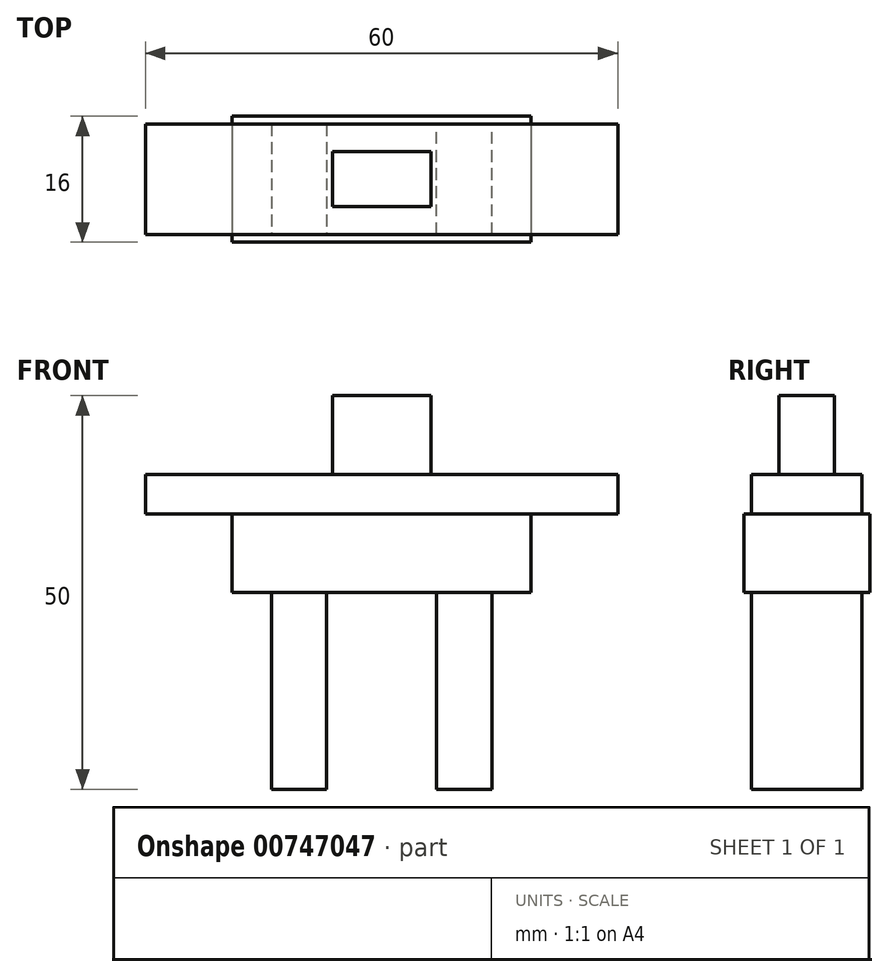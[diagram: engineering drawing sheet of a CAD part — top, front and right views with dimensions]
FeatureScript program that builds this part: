
annotation { "Feature Type Name" : "Feature", "Feature Type Description" : "" }
export const myFeature = defineFeature(function(context is Context, id is Id, definition is map)
    precondition{}
    {
        {
            var Q0;
            Q0=qCreatedBy(makeId("Top.planeOp"),FACE);
            var sketch = newSketch(context, id + "F0", { "sketchPlane" : qUnion([Q0])});
            skLineSegment(sketch, "E0.bottom", {"start": v(-14, 7) * mm, "end": v(-7, 7) * mm});
            skLineSegment(sketch, "E0.top", {"start": v(-14, -7) * mm, "end": v(-7, -7) * mm});
            skLineSegment(sketch, "E0.left", {"start": v(-14, 7) * mm, "end": v(-14, -7) * mm});
            skLineSegment(sketch, "E0.right", {"start": v(-7, 7) * mm, "end": v(-7, -7) * mm});
            skPoint(sketch, "E1", {"position": v(-14, 0) * mm});
            skSolve(sketch);
        }
        {
            var Q0;
            Q0 = qSketchRegion(id + "F0", true);
            extrude(context, id + "F1", {"entities" : qUnion([Q0]), "depth" : 25 * mm, "offsetDistance" : 25.4 * mm});
        }
        {
            var Q0;
            Q0=makeQuery(id+"F1.opExtrude","CAP_FACE",FACE,{"disambiguationData":[OSD([sQuery(id+"F0.wireOp",EDGE,"E0.bottom"),sQuery(id+"F0.wireOp",EDGE,"E0.top"),sQuery(id+"F0.wireOp",EDGE,"E0.left"),sQuery(id+"F0.wireOp",EDGE,"E0.right")])],"isStart":false});
            var sketch = newSketch(context, id + "F2", { "sketchPlane" : qUnion([Q0])});
            skLineSegment(sketch, "E2.bottom", {"start": v(-19, 8) * mm, "end": v(19, 8) * mm});
            skLineSegment(sketch, "E2.top", {"start": v(-19, -8) * mm, "end": v(19, -8) * mm});
            skLineSegment(sketch, "E2.left", {"start": v(-19, 8) * mm, "end": v(-19, -8) * mm});
            skLineSegment(sketch, "E2.right", {"start": v(19, 8) * mm, "end": v(19, -8) * mm});
            skPoint(sketch, "E3", {"position": v(0, 8) * mm});
            skPoint(sketch, "E4", {"position": v(-19, 0) * mm});
            skSolve(sketch);
        }
        {
            var Q0;
            Q0 = qSketchRegion(id + "F2", true);
            extrude(context, id + "F3", {"entities" : qUnion([Q0]), "operationType" : NewBodyOperationType.ADD, "depth" : 10 * mm, "offsetDistance" : 25 * mm});
        }
        {
            var Q0;
            Q0=makeQuery(id+"F3.opExtrude","CAP_FACE",FACE,{"disambiguationData":[OSD([sQuery(id+"F2.wireOp",EDGE,"E2.bottom"),sQuery(id+"F2.wireOp",EDGE,"E2.top"),sQuery(id+"F2.wireOp",EDGE,"E2.left"),sQuery(id+"F2.wireOp",EDGE,"E2.right")])],"isStart":false});
            var sketch = newSketch(context, id + "F4", { "sketchPlane" : qUnion([Q0])});
            skLineSegment(sketch, "E5.bottom", {"start": v(-30, 7) * mm, "end": v(30, 7) * mm});
            skLineSegment(sketch, "E5.top", {"start": v(-30, -7) * mm, "end": v(30, -7) * mm});
            skLineSegment(sketch, "E5.left", {"start": v(-30, 7) * mm, "end": v(-30, -7) * mm});
            skLineSegment(sketch, "E5.right", {"start": v(30, 7) * mm, "end": v(30, -7) * mm});
            skPoint(sketch, "E6", {"position": v(0, 7) * mm});
            skPoint(sketch, "E7", {"position": v(30, 0) * mm});
            skSolve(sketch);
        }
        {
            var Q0;
            Q0 = qSketchRegion(id + "F4", true);
            extrude(context, id + "F5", {"entities" : qUnion([Q0]), "operationType" : NewBodyOperationType.ADD, "depth" : 5 * mm, "offsetDistance" : 25 * mm});
        }
        {
            var Q0;
            Q0=makeQuery(id+"F5.opExtrude","CAP_FACE",FACE,{"disambiguationData":[OSD([sQuery(id+"F4.wireOp",EDGE,"E5.bottom"),sQuery(id+"F4.wireOp",EDGE,"E5.top"),sQuery(id+"F4.wireOp",EDGE,"E5.left"),sQuery(id+"F4.wireOp",EDGE,"E5.right")])],"isStart":false});
            var sketch = newSketch(context, id + "F6", { "sketchPlane" : qUnion([Q0])});
            skLineSegment(sketch, "E8.bottom", {"start": v(-6.25, 3.5) * mm, "end": v(6.25, 3.5) * mm});
            skLineSegment(sketch, "E8.top", {"start": v(-6.25, -3.5) * mm, "end": v(6.25, -3.5) * mm});
            skLineSegment(sketch, "E8.left", {"start": v(-6.25, 3.5) * mm, "end": v(-6.25, -3.5) * mm});
            skLineSegment(sketch, "E8.right", {"start": v(6.25, 3.5) * mm, "end": v(6.25, -3.5) * mm});
            skPoint(sketch, "E9", {"position": v(0, 3.5) * mm});
            skPoint(sketch, "E10", {"position": v(6.25, 0) * mm});
            skSolve(sketch);
        }
        {
            var Q0;
            Q0 = qSketchRegion(id + "F6", true);
            extrude(context, id + "F7", {"entities" : qUnion([Q0]), "operationType" : NewBodyOperationType.ADD, "depth" : 10 * mm, "offsetDistance" : 25 * mm});
        }
        {
            var Q0;
            Q0=makeQuery(id+"F3.opExtrude","CAP_FACE",FACE,{"disambiguationData":[OSD([sQuery(id+"F2.wireOp",EDGE,"E2.bottom"),sQuery(id+"F2.wireOp",EDGE,"E2.top"),sQuery(id+"F2.wireOp",EDGE,"E2.left"),sQuery(id+"F2.wireOp",EDGE,"E2.right")])],"isStart":true});
            var sketch = newSketch(context, id + "F8", { "sketchPlane" : qUnion([Q0])});
            skLineSegment(sketch, "E11.bottom", {"start": v(7, 7) * mm, "end": v(14, 7) * mm});
            skLineSegment(sketch, "E11.top", {"start": v(7, -7) * mm, "end": v(14, -7) * mm});
            skLineSegment(sketch, "E11.left", {"start": v(7, 7) * mm, "end": v(7, -7) * mm});
            skLineSegment(sketch, "E11.right", {"start": v(14, 7) * mm, "end": v(14, -7) * mm});
            skLineSegment(sketch, "E12", {"start": v(-7, 7) * mm, "end": v(0, 7) * mm, "construction": true});
            skLineSegment(sketch, "E13", {"start": v(0, 7) * mm, "end": v(7, 7) * mm, "construction": true});
            skSolve(sketch);
        }
        {
            var Q0;
            Q0 = qSketchRegion(id + "F8", true);
            var Q1;
            Q1=makeQuery(id+"F1.opExtrude","CAP_FACE",FACE,{"disambiguationData":[OSD([sQuery(id+"F0.wireOp",EDGE,"E0.bottom"),sQuery(id+"F0.wireOp",EDGE,"E0.top"),sQuery(id+"F0.wireOp",EDGE,"E0.left"),sQuery(id+"F0.wireOp",EDGE,"E0.right")])],"isStart":true});
            extrude(context, id + "F9", {"entities" : qUnion([Q0]), "operationType" : NewBodyOperationType.ADD, "endBound" : BoundingType.UP_TO_SURFACE, "depth" : 25 * mm, "endBoundEntityFace" : qUnion([Q1]), "offsetDistance" : 25 * mm});
        }
    });
